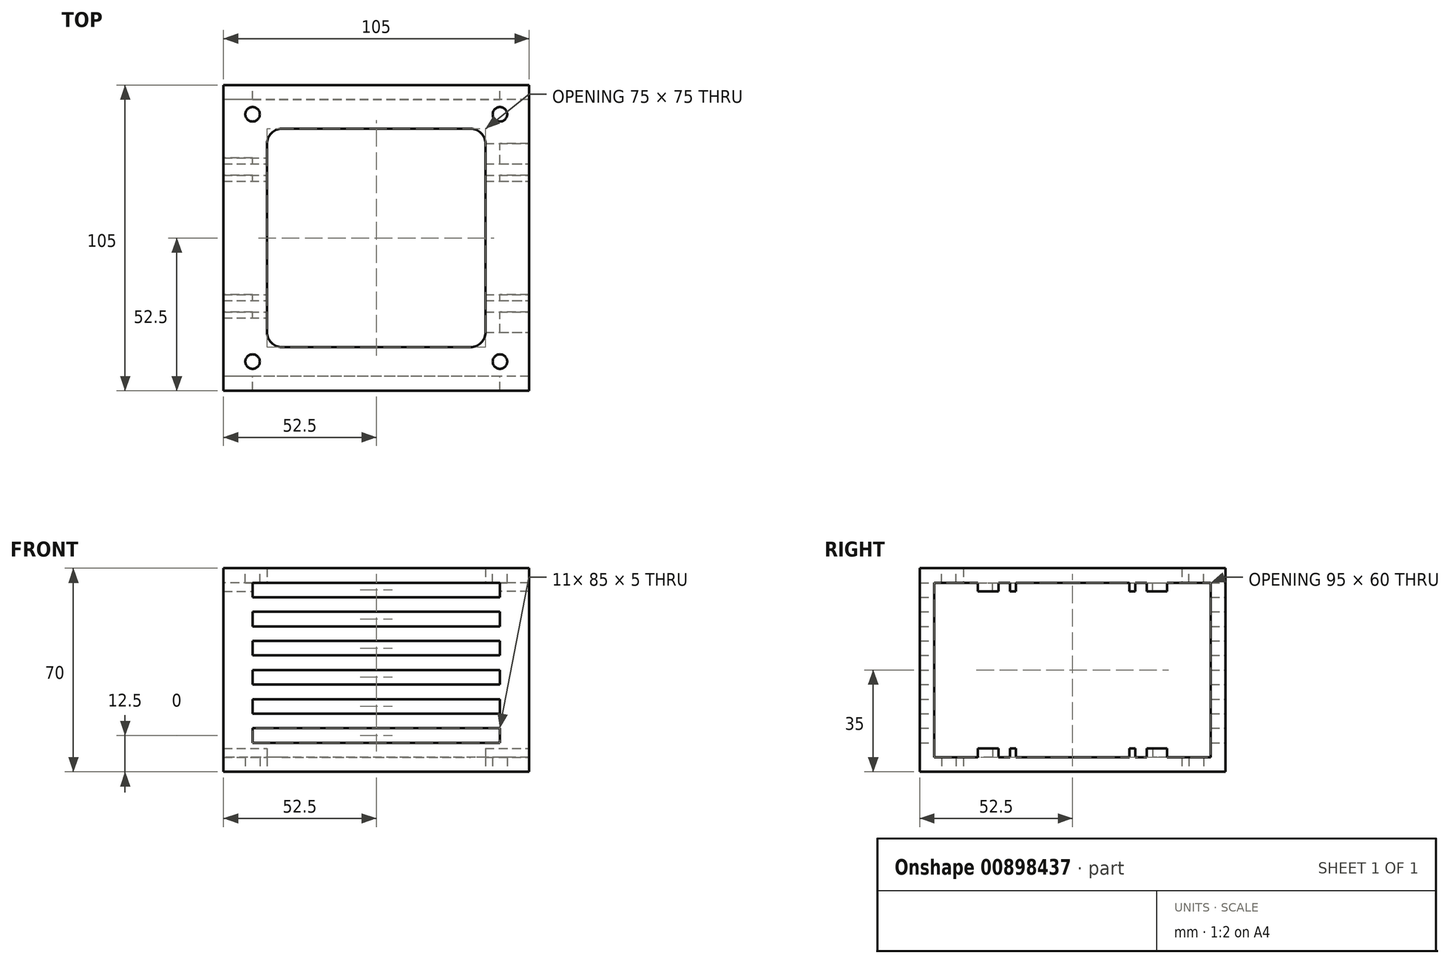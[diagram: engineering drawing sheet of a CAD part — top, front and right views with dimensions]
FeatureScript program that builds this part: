
annotation { "Feature Type Name" : "Feature", "Feature Type Description" : "" }
export const myFeature = defineFeature(function(context is Context, id is Id, definition is map)
    precondition{}
    {
        {
            var Q0;
            Q0=qCreatedBy(makeId("Top.planeOp"),FACE);
            var sketch = newSketch(context, id + "F0", { "sketchPlane" : qUnion([Q0])});
            skLineSegment(sketch, "E0.bottom", {"start": v(-52.5, 52.5) * mm, "end": v(52.5, 52.5) * mm});
            skLineSegment(sketch, "E0.top", {"start": v(-52.5, -52.5) * mm, "end": v(52.5, -52.5) * mm});
            skLineSegment(sketch, "E0.left", {"start": v(-52.5, 52.5) * mm, "end": v(-52.5, -52.5) * mm});
            skLineSegment(sketch, "E0.right", {"start": v(52.5, 52.5) * mm, "end": v(52.5, -52.5) * mm});
            skCircle(sketch, "E1", {"center": v(-42.5, 42.5) * mm, "radius": 2.5 * mm});
            skCircle(sketch, "E2.MirrorC", {"center": v(42.5, 42.5) * mm, "radius": 2.5 * mm});
            skCircle(sketch, "E3.MirrorC", {"center": v(-42.5, -42.5) * mm, "radius": 2.5 * mm});
            skCircle(sketch, "E4.MirrorC", {"center": v(42.5, -42.5) * mm, "radius": 2.5 * mm});
            skLineSegment(sketch, "E5.bottom", {"start": v(-32.5, 37.5) * mm, "end": v(32.5, 37.5) * mm});
            skLineSegment(sketch, "E5.top", {"start": v(-32.5, -37.5) * mm, "end": v(32.5, -37.5) * mm});
            skLineSegment(sketch, "E5.left", {"start": v(-37.5, 32.5) * mm, "end": v(-37.5, -32.5) * mm});
            skLineSegment(sketch, "E5.right", {"start": v(37.5, 32.5) * mm, "end": v(37.5, -32.5) * mm});
            skPoint(sketch, "E6.visualSharp", {"position": v(-37.5, 37.5) * mm});
            skArc(sketch, "E6.filletArc", {"start": v(-32.5, 37.5) * mm, "mid": v(-36.04, 36.04) * mm, "end": v(-37.5, 32.5) * mm});
            skPoint(sketch, "E7.visualSharp", {"position": v(-37.5, -37.5) * mm});
            skArc(sketch, "E7.filletArc", {"start": v(-37.5, -32.5) * mm, "mid": v(-36.04, -36.04) * mm, "end": v(-32.5, -37.5) * mm});
            skPoint(sketch, "E8.visualSharp", {"position": v(37.5, -37.5) * mm});
            skArc(sketch, "E8.filletArc", {"start": v(32.5, -37.5) * mm, "mid": v(36.04, -36.04) * mm, "end": v(37.5, -32.5) * mm});
            skPoint(sketch, "E9.visualSharp", {"position": v(37.5, 37.5) * mm});
            skArc(sketch, "E9.filletArc", {"start": v(37.5, 32.5) * mm, "mid": v(36.04, 36.04) * mm, "end": v(32.5, 37.5) * mm});
            skSolve(sketch);
        }
        {
            var Q0;
            Q0=makeQuery(id+"F0.imprint","IMPRINT",FACE,{"disambiguationData":[TD([[makeQuery(id+"F0.imprint","IMPRINT",EDGE,{"derivedFrom":sQuery(id+"F0.wireOp",EDGE,"E0.bottom")}),-1.0]])]});
            extrude(context, id + "F1", {"entities" : qUnion([Q0]), "depth" : 5 * mm, "offsetDistance" : 25 * mm});
        }
        {
            var Q0;
            Q0=makeQuery(id+"F1.opExtrude","CAP_FACE",FACE,{"disambiguationData":[OSD([sQuery(id+"F0.wireOp",EDGE,"E0.bottom"),sQuery(id+"F0.wireOp",EDGE,"E0.top"),sQuery(id+"F0.wireOp",EDGE,"E0.left"),sQuery(id+"F0.wireOp",EDGE,"E0.right"),sQuery(id+"F0.wireOp",EDGE,"E2.MirrorC"),sQuery(id+"F0.wireOp",EDGE,"E1"),sQuery(id+"F0.wireOp",EDGE,"E3.MirrorC"),sQuery(id+"F0.wireOp",EDGE,"E4.MirrorC"),sQuery(id+"F0.wireOp",EDGE,"E5.bottom"),sQuery(id+"F0.wireOp",EDGE,"E5.top"),sQuery(id+"F0.wireOp",EDGE,"E5.left"),sQuery(id+"F0.wireOp",EDGE,"E5.right"),sQuery(id+"F0.wireOp",EDGE,"E6.filletArc"),sQuery(id+"F0.wireOp",EDGE,"E7.filletArc"),sQuery(id+"F0.wireOp",EDGE,"E8.filletArc"),sQuery(id+"F0.wireOp",EDGE,"E9.filletArc")])],"isStart":false});
            var sketch = newSketch(context, id + "F2", { "sketchPlane" : qUnion([Q0])});
            skLineSegment(sketch, "E10.bottom", {"start": v(-52.5, 27.5) * mm, "end": v(-37.5, 27.5) * mm});
            skLineSegment(sketch, "E10.top", {"start": v(-52.5, 25.5) * mm, "end": v(-37.5, 25.5) * mm});
            skLineSegment(sketch, "E10.left", {"start": v(-52.5, 27.5) * mm, "end": v(-52.5, 25.5) * mm});
            skLineSegment(sketch, "E10.right", {"start": v(52.5, 32.5) * mm, "end": v(52.5, 25.5) * mm});
            skLineSegment(sketch, "E11.0", {"start": v(37.5, 32.5) * mm, "end": v(37.5, 25.5) * mm});
            skLineSegment(sketch, "E12.0", {"start": v(-37.5, 27.5) * mm, "end": v(-37.5, 25.5) * mm});
            skLineSegment(sketch, "E13.trimOffspring", {"start": v(37.5, 32.5) * mm, "end": v(52.5, 32.5) * mm});
            skLineSegment(sketch, "E14.trimOffspring", {"start": v(37.5, 25.5) * mm, "end": v(52.5, 25.5) * mm});
            skLineSegment(sketch, "E15.bottom", {"start": v(-52.5, 21.5) * mm, "end": v(-37.5, 21.5) * mm});
            skLineSegment(sketch, "E15.top", {"start": v(-52.5, 19.5) * mm, "end": v(-37.5, 19.5) * mm});
            skLineSegment(sketch, "E15.left", {"start": v(-52.5, 21.5) * mm, "end": v(-52.5, 19.5) * mm});
            skLineSegment(sketch, "E15.right", {"start": v(52.5, 21.5) * mm, "end": v(52.5, 19.5) * mm});
            skLineSegment(sketch, "E16.trimOffspring", {"start": v(37.5, 21.5) * mm, "end": v(52.5, 21.5) * mm});
            skLineSegment(sketch, "E17.trimOffspring", {"start": v(37.5, 19.5) * mm, "end": v(52.5, 19.5) * mm});
            skLineSegment(sketch, "E18.MirrorCS", {"start": v(-52.5, -27.5) * mm, "end": v(-37.5, -27.5) * mm});
            skLineSegment(sketch, "E19.MirrorCS", {"start": v(-52.5, -25.5) * mm, "end": v(-37.5, -25.5) * mm});
            skLineSegment(sketch, "E20.MirrorCS", {"start": v(-52.5, -21.5) * mm, "end": v(-37.5, -21.5) * mm});
            skLineSegment(sketch, "E21.MirrorCS", {"start": v(-52.5, -19.5) * mm, "end": v(-37.5, -19.5) * mm});
            skLineSegment(sketch, "E22.MirrorCS", {"start": v(37.5, -32.5) * mm, "end": v(52.5, -32.5) * mm});
            skLineSegment(sketch, "E23.MirrorCS", {"start": v(37.5, -25.5) * mm, "end": v(52.5, -25.5) * mm});
            skLineSegment(sketch, "E24.MirrorCS", {"start": v(37.5, -21.5) * mm, "end": v(52.5, -21.5) * mm});
            skLineSegment(sketch, "E25.MirrorCS", {"start": v(37.5, -19.5) * mm, "end": v(52.5, -19.5) * mm});
            skLineSegment(sketch, "E26.MirrorCS", {"start": v(37.5, -32.5) * mm, "end": v(37.5, -25.5) * mm});
            skLineSegment(sketch, "E27.MirrorCS", {"start": v(52.5, -21.5) * mm, "end": v(52.5, -19.5) * mm});
            skLineSegment(sketch, "E28.MirrorCS", {"start": v(52.5, -32.5) * mm, "end": v(52.5, -25.5) * mm});
            skLineSegment(sketch, "E29.MirrorCS", {"start": v(-52.5, -27.5) * mm, "end": v(-52.5, -25.5) * mm});
            skLineSegment(sketch, "E30.MirrorCS", {"start": v(-52.5, -21.5) * mm, "end": v(-52.5, -19.5) * mm});
            skLineSegment(sketch, "E31.MirrorCS", {"start": v(-37.5, -27.5) * mm, "end": v(-37.5, -25.5) * mm});
            skLineSegment(sketch, "E32.trimOffspring", {"start": v(-37.5, 21.5) * mm, "end": v(-37.5, 19.5) * mm});
            skLineSegment(sketch, "E33.trimOffspring", {"start": v(37.5, 21.5) * mm, "end": v(37.5, 19.5) * mm});
            skLineSegment(sketch, "E34.trimOffspring", {"start": v(37.5, -21.5) * mm, "end": v(37.5, -19.5) * mm});
            skLineSegment(sketch, "E35.trimOffspring", {"start": v(-37.5, -21.5) * mm, "end": v(-37.5, -19.5) * mm});
            skSolve(sketch);
        }
        {
            var Q0;
            Q0=makeQuery(id+"F2.imprint","IMPRINT",FACE,{"disambiguationData":[TD([[makeQuery(id+"F2.imprint","IMPRINT",EDGE,{"derivedFrom":sQuery(id+"F2.wireOp",EDGE,"E10.bottom")}),-1.0]])]});
            var Q1;
            Q1=makeQuery(id+"F2.imprint","IMPRINT",FACE,{"disambiguationData":[TD([[makeQuery(id+"F2.imprint","IMPRINT",EDGE,{"derivedFrom":sQuery(id+"F2.wireOp",EDGE,"E15.bottom")}),-1.0]])]});
            var Q2;
            Q2=makeQuery(id+"F2.imprint","IMPRINT",FACE,{"disambiguationData":[TD([[makeQuery(id+"F2.imprint","IMPRINT",EDGE,{"derivedFrom":sQuery(id+"F2.wireOp",EDGE,"E15.right")}),-1.0]])]});
            var Q3;
            Q3=makeQuery(id+"F2.imprint","IMPRINT",FACE,{"disambiguationData":[TD([[makeQuery(id+"F2.imprint","IMPRINT",EDGE,{"derivedFrom":sQuery(id+"F2.wireOp",EDGE,"E10.right")}),-1.0]])]});
            var Q4;
            Q4=makeQuery(id+"F2.imprint","IMPRINT",FACE,{"disambiguationData":[TD([[makeQuery(id+"F2.imprint","IMPRINT",EDGE,{"derivedFrom":sQuery(id+"F2.wireOp",EDGE,"E24.MirrorCS")}),1.0]])]});
            var Q5;
            Q5=makeQuery(id+"F2.imprint","IMPRINT",FACE,{"disambiguationData":[TD([[makeQuery(id+"F2.imprint","IMPRINT",EDGE,{"derivedFrom":sQuery(id+"F2.wireOp",EDGE,"E22.MirrorCS")}),1.0]])]});
            var Q6;
            Q6=makeQuery(id+"F2.imprint","IMPRINT",FACE,{"disambiguationData":[TD([[makeQuery(id+"F2.imprint","IMPRINT",EDGE,{"derivedFrom":sQuery(id+"F2.wireOp",EDGE,"E18.MirrorCS")}),1.0]])]});
            var Q7;
            Q7=makeQuery(id+"F2.imprint","IMPRINT",FACE,{"disambiguationData":[TD([[makeQuery(id+"F2.imprint","IMPRINT",EDGE,{"derivedFrom":sQuery(id+"F2.wireOp",EDGE,"E20.MirrorCS")}),1.0]])]});
            extrude(context, id + "F3", {"entities" : qUnion([Q0, Q1, Q2, Q3, Q4, Q5, Q6, Q7]), "operationType" : NewBodyOperationType.ADD, "depth" : 3 * mm, "offsetDistance" : 25 * mm});
        }
        {
            var Q0;
            Q0=qCreatedBy(makeId("Right.planeOp"),FACE);
            var sketch = newSketch(context, id + "F4", { "sketchPlane" : qUnion([Q0])});
            skLineSegment(sketch, "E36.0.4", {"start": v(52.5, 5) * mm, "end": v(47.5, 5) * mm});
            skLineSegment(sketch, "E37.0.7", {"start": v(-52.5, 5) * mm, "end": v(-47.5, 5) * mm});
            skLineSegment(sketch, "E38", {"start": v(52.5, 5) * mm, "end": v(52.5, 70) * mm});
            skLineSegment(sketch, "E39", {"start": v(52.5, 70) * mm, "end": v(-52.5, 70) * mm});
            skLineSegment(sketch, "E40", {"start": v(-52.5, 70) * mm, "end": v(-52.5, 5) * mm});
            skLineSegment(sketch, "E41", {"start": v(-47.5, 5) * mm, "end": v(-47.5, 65) * mm});
            skLineSegment(sketch, "E42", {"start": v(-47.5, 65) * mm, "end": v(47.5, 65) * mm});
            skLineSegment(sketch, "E43", {"start": v(47.5, 65) * mm, "end": v(47.5, 5) * mm});
            skLineSegment(sketch, "E44.trimOffspring", {"start": v(-47.5, 5) * mm, "end": v(-52.5, 5) * mm});
            skSolve(sketch);
        }
        {
            var Q0;
            Q0=makeQuery(id+"F4.imprint","IMPRINT",FACE,{"disambiguationData":[TD([[makeQuery(id+"F4.imprint","IMPRINT",EDGE,{"derivedFrom":sQuery(id+"F4.wireOp",EDGE,"E36.0.4")}),-1.0]])]});
            extrude(context, id + "F5", {"entities" : qUnion([Q0]), "operationType" : NewBodyOperationType.ADD, "depth" : (105 / 2) * mm, "offsetDistance" : 25 * mm, "hasSecondDirection" : true, "secondDirectionOppositeDirection" : true, "secondDirectionDepth" : 52.5 * mm});
        }
        {
            var Q0;
            Q0=makeQuery(id+"F5.opExtrude","SWEPT_FACE",FACE,{"disambiguationData":[OSD([sQuery(id+"F4.wireOp",EDGE,"E42")])]});
            var sketch = newSketch(context, id + "F6", { "sketchPlane" : qUnion([Q0])});
            skLineSegment(sketch, "E45.0", {"start": v(-32.5, -37.5) * mm, "end": v(32.5, -37.5) * mm});
            skArc(sketch, "E46.0", {"start": v(-32.5, -37.5) * mm, "mid": v(-36.04, -36.04) * mm, "end": v(-37.5, -32.5) * mm});
            skLineSegment(sketch, "E47.0", {"start": v(-37.5, -32.5) * mm, "end": v(-37.5, 32.5) * mm});
            skLineSegment(sketch, "E48.0", {"start": v(-32.5, 37.5) * mm, "end": v(32.5, 37.5) * mm});
            skArc(sketch, "E49.0", {"start": v(37.5, -32.5) * mm, "mid": v(36.04, -36.04) * mm, "end": v(32.5, -37.5) * mm});
            skArc(sketch, "E50.0", {"start": v(32.5, 37.5) * mm, "mid": v(36.04, 36.04) * mm, "end": v(37.5, 32.5) * mm});
            skArc(sketch, "E51.0", {"start": v(-37.5, 32.5) * mm, "mid": v(-36.04, 36.04) * mm, "end": v(-32.5, 37.5) * mm});
            skLineSegment(sketch, "E52.0", {"start": v(37.5, -32.5) * mm, "end": v(37.5, 32.5) * mm});
            skSolve(sketch);
        }
        {
            var Q0;
            Q0=makeQuery(id+"F6.imprint","IMPRINT",FACE,{"disambiguationData":[TD([[makeQuery(id+"F6.imprint","IMPRINT",EDGE,{"derivedFrom":sQuery(id+"F6.wireOp",EDGE,"E45.0")}),1.0]])]});
            extrude(context, id + "F7", {"entities" : qUnion([Q0]), "operationType" : NewBodyOperationType.REMOVE, "endBound" : BoundingType.UP_TO_NEXT, "oppositeDirection" : true, "depth" : 25 * mm, "offsetDistance" : 25 * mm});
        }
        {
            var Q0;
            Q0=makeQuery(id+"F5.opExtrude","SWEPT_FACE",FACE,{"disambiguationData":[OSD([sQuery(id+"F4.wireOp",EDGE,"E42")])]});
            var sketch = newSketch(context, id + "F8", { "sketchPlane" : qUnion([Q0])});
            skLineSegment(sketch, "E53.0.0", {"start": v(-52.5, -27.5) * mm, "end": v(-52.5, -25.5) * mm});
            skLineSegment(sketch, "E53.0.1", {"start": v(-52.5, -25.5) * mm, "end": v(-37.5, -25.5) * mm});
            skLineSegment(sketch, "E53.0.2", {"start": v(-37.5, -25.5) * mm, "end": v(-37.5, -27.5) * mm});
            skLineSegment(sketch, "E53.0.3", {"start": v(-37.5, -27.5) * mm, "end": v(-52.5, -27.5) * mm});
            skLineSegment(sketch, "E54.0.0", {"start": v(-52.5, -21.5) * mm, "end": v(-52.5, -19.5) * mm});
            skLineSegment(sketch, "E54.0.1", {"start": v(-52.5, -19.5) * mm, "end": v(-37.5, -19.5) * mm});
            skLineSegment(sketch, "E54.0.2", {"start": v(-37.5, -19.5) * mm, "end": v(-37.5, -21.5) * mm});
            skLineSegment(sketch, "E54.0.3", {"start": v(-37.5, -21.5) * mm, "end": v(-52.5, -21.5) * mm});
            skLineSegment(sketch, "E55.0.0", {"start": v(-37.5, 19.5) * mm, "end": v(-52.5, 19.5) * mm});
            skLineSegment(sketch, "E55.0.1", {"start": v(-52.5, 19.5) * mm, "end": v(-52.5, 21.5) * mm});
            skLineSegment(sketch, "E55.0.2", {"start": v(-52.5, 21.5) * mm, "end": v(-37.5, 21.5) * mm});
            skLineSegment(sketch, "E55.0.3", {"start": v(-37.5, 21.5) * mm, "end": v(-37.5, 19.5) * mm});
            skLineSegment(sketch, "E56.0.0", {"start": v(-37.5, 25.5) * mm, "end": v(-52.5, 25.5) * mm});
            skLineSegment(sketch, "E56.0.1", {"start": v(-52.5, 25.5) * mm, "end": v(-52.5, 27.5) * mm});
            skLineSegment(sketch, "E56.0.2", {"start": v(-52.5, 27.5) * mm, "end": v(-37.5, 27.5) * mm});
            skLineSegment(sketch, "E56.0.3", {"start": v(-37.5, 27.5) * mm, "end": v(-37.5, 25.5) * mm});
            skLineSegment(sketch, "E57.0.0", {"start": v(52.5, 25.5) * mm, "end": v(37.5, 25.5) * mm});
            skLineSegment(sketch, "E57.0.1", {"start": v(37.5, 25.5) * mm, "end": v(37.5, 32.5) * mm});
            skLineSegment(sketch, "E57.0.2", {"start": v(37.5, 32.5) * mm, "end": v(52.5, 32.5) * mm});
            skLineSegment(sketch, "E57.0.3", {"start": v(52.5, 32.5) * mm, "end": v(52.5, 25.5) * mm});
            skLineSegment(sketch, "E58.0.0", {"start": v(52.5, 19.5) * mm, "end": v(37.5, 19.5) * mm});
            skLineSegment(sketch, "E58.0.1", {"start": v(37.5, 19.5) * mm, "end": v(37.5, 21.5) * mm});
            skLineSegment(sketch, "E58.0.2", {"start": v(37.5, 21.5) * mm, "end": v(52.5, 21.5) * mm});
            skLineSegment(sketch, "E58.0.3", {"start": v(52.5, 21.5) * mm, "end": v(52.5, 19.5) * mm});
            skLineSegment(sketch, "E59.0.0", {"start": v(37.5, -32.5) * mm, "end": v(37.5, -25.5) * mm});
            skLineSegment(sketch, "E59.0.1", {"start": v(37.5, -25.5) * mm, "end": v(52.5, -25.5) * mm});
            skLineSegment(sketch, "E59.0.2", {"start": v(52.5, -25.5) * mm, "end": v(52.5, -32.5) * mm});
            skLineSegment(sketch, "E59.0.3", {"start": v(52.5, -32.5) * mm, "end": v(37.5, -32.5) * mm});
            skLineSegment(sketch, "E60.0.0", {"start": v(37.5, -21.5) * mm, "end": v(37.5, -19.5) * mm});
            skLineSegment(sketch, "E60.0.1", {"start": v(37.5, -19.5) * mm, "end": v(52.5, -19.5) * mm});
            skLineSegment(sketch, "E60.0.2", {"start": v(52.5, -19.5) * mm, "end": v(52.5, -21.5) * mm});
            skLineSegment(sketch, "E60.0.3", {"start": v(52.5, -21.5) * mm, "end": v(37.5, -21.5) * mm});
            skSolve(sketch);
        }
        {
            var Q0;
            Q0 = qSketchRegion(id + "F8", true);
            extrude(context, id + "F9", {"entities" : qUnion([Q0]), "operationType" : NewBodyOperationType.ADD, "depth" : 3 * mm, "offsetDistance" : 25 * mm});
        }
        {
            var Q0;
            Q0=makeQuery(id+"F5.boolean.opBoolean","MERGE",FACE,{"derivedFrom":[makeQuery(id+"F1.opExtrude","SWEPT_FACE",FACE,{"disambiguationData":[OSD([sQuery(id+"F0.wireOp",EDGE,"E0.bottom")])]}),makeQuery(id+"F5.opExtrude","SWEPT_FACE",FACE,{"disambiguationData":[OSD([sQuery(id+"F4.wireOp",EDGE,"E38")])]})]});
            var sketch = newSketch(context, id + "F10", { "sketchPlane" : qUnion([Q0])});
            skLineSegment(sketch, "E61.bottom", {"start": v(42.5, 10) * mm, "end": v(-42.5, 10) * mm});
            skLineSegment(sketch, "E61.top", {"start": v(42.5, 15) * mm, "end": v(-42.5, 15) * mm});
            skLineSegment(sketch, "E61.left", {"start": v(42.5, 10) * mm, "end": v(42.5, 15) * mm});
            skLineSegment(sketch, "E61.right", {"start": v(-42.5, 10) * mm, "end": v(-42.5, 15) * mm});
            skLineSegment(sketch, "E62.0.1.0", {"start": v(42.5, 20) * mm, "end": v(-42.5, 20) * mm});
            skLineSegment(sketch, "E62.0.1.1", {"start": v(42.5, 25) * mm, "end": v(-42.5, 25) * mm});
            skLineSegment(sketch, "E62.0.1.2", {"start": v(42.5, 20) * mm, "end": v(42.5, 25) * mm});
            skLineSegment(sketch, "E62.0.1.3", {"start": v(-42.5, 20) * mm, "end": v(-42.5, 25) * mm});
            skLineSegment(sketch, "E62.0.2.0", {"start": v(42.5, 30) * mm, "end": v(-42.5, 30) * mm});
            skLineSegment(sketch, "E62.0.2.1", {"start": v(42.5, 35) * mm, "end": v(-42.5, 35) * mm});
            skLineSegment(sketch, "E62.0.2.2", {"start": v(42.5, 30) * mm, "end": v(42.5, 35) * mm});
            skLineSegment(sketch, "E62.0.2.3", {"start": v(-42.5, 30) * mm, "end": v(-42.5, 35) * mm});
            skLineSegment(sketch, "E62.0.3.0", {"start": v(42.5, 40) * mm, "end": v(-42.5, 40) * mm});
            skLineSegment(sketch, "E62.0.3.1", {"start": v(42.5, 45) * mm, "end": v(-42.5, 45) * mm});
            skLineSegment(sketch, "E62.0.3.2", {"start": v(42.5, 40) * mm, "end": v(42.5, 45) * mm});
            skLineSegment(sketch, "E62.0.3.3", {"start": v(-42.5, 40) * mm, "end": v(-42.5, 45) * mm});
            skLineSegment(sketch, "E62.0.4.0", {"start": v(42.5, 50) * mm, "end": v(-42.5, 50) * mm});
            skLineSegment(sketch, "E62.0.4.1", {"start": v(42.5, 55) * mm, "end": v(-42.5, 55) * mm});
            skLineSegment(sketch, "E62.0.4.2", {"start": v(42.5, 50) * mm, "end": v(42.5, 55) * mm});
            skLineSegment(sketch, "E62.0.4.3", {"start": v(-42.5, 50) * mm, "end": v(-42.5, 55) * mm});
            skLineSegment(sketch, "E62.0.5.0", {"start": v(42.5, 60) * mm, "end": v(-42.5, 60) * mm});
            skLineSegment(sketch, "E62.0.5.1", {"start": v(42.5, 65) * mm, "end": v(-42.5, 65) * mm});
            skLineSegment(sketch, "E62.0.5.2", {"start": v(42.5, 60) * mm, "end": v(42.5, 65) * mm});
            skLineSegment(sketch, "E62.0.5.3", {"start": v(-42.5, 60) * mm, "end": v(-42.5, 65) * mm});
            skLineSegment(sketch, "E62.direction1", {"start": v(-42.5, 10) * mm, "end": v(-17.5, 10) * mm, "construction": true});
            skLineSegment(sketch, "E62.direction2", {"start": v(-42.5, 10) * mm, "end": v(-42.5, 20) * mm, "construction": true});
            skSolve(sketch);
        }
        {
            var Q0;
            Q0=makeQuery(id+"F10.imprint","IMPRINT",FACE,{"disambiguationData":[TD([[makeQuery(id+"F10.imprint","IMPRINT",EDGE,{"derivedFrom":sQuery(id+"F10.wireOp",EDGE,"E61.bottom")}),-1.0]])]});
            var Q1;
            Q1=makeQuery(id+"F10.imprint","IMPRINT",FACE,{"disambiguationData":[TD([[makeQuery(id+"F10.imprint","IMPRINT",EDGE,{"derivedFrom":sQuery(id+"F10.wireOp",EDGE,"E62.0.1.0")}),-1.0]])]});
            var Q2;
            Q2=makeQuery(id+"F10.imprint","IMPRINT",FACE,{"disambiguationData":[TD([[makeQuery(id+"F10.imprint","IMPRINT",EDGE,{"derivedFrom":sQuery(id+"F10.wireOp",EDGE,"E62.0.2.0")}),-1.0]])]});
            var Q3;
            Q3=makeQuery(id+"F10.imprint","IMPRINT",FACE,{"disambiguationData":[TD([[makeQuery(id+"F10.imprint","IMPRINT",EDGE,{"derivedFrom":sQuery(id+"F10.wireOp",EDGE,"E62.0.3.0")}),-1.0]])]});
            var Q4;
            Q4=makeQuery(id+"F10.imprint","IMPRINT",FACE,{"disambiguationData":[TD([[makeQuery(id+"F10.imprint","IMPRINT",EDGE,{"derivedFrom":sQuery(id+"F10.wireOp",EDGE,"E62.0.4.0")}),-1.0]])]});
            var Q5;
            Q5=makeQuery(id+"F10.imprint","IMPRINT",FACE,{"disambiguationData":[TD([[makeQuery(id+"F10.imprint","IMPRINT",EDGE,{"derivedFrom":sQuery(id+"F10.wireOp",EDGE,"E62.0.5.0")}),-1.0]])]});
            extrude(context, id + "F11", {"entities" : qUnion([Q0, Q1, Q2, Q3, Q4, Q5]), "operationType" : NewBodyOperationType.REMOVE, "endBound" : BoundingType.THROUGH_ALL, "oppositeDirection" : true, "depth" : 25 * mm, "offsetDistance" : 25 * mm});
        }
        {
            var Q0;
            Q0=makeQuery(id+"F5.opExtrude","SWEPT_FACE",FACE,{"disambiguationData":[OSD([sQuery(id+"F4.wireOp",EDGE,"E39")])]});
            var sketch = newSketch(context, id + "F12", { "sketchPlane" : qUnion([Q0])});
            skCircle(sketch, "E63.0", {"center": v(-42.5, 42.5) * mm, "radius": 2.5 * mm});
            skCircle(sketch, "E63.1", {"center": v(-42.5, -42.5) * mm, "radius": 2.5 * mm});
            skCircle(sketch, "E63.2", {"center": v(42.5, 42.5) * mm, "radius": 2.5 * mm});
            skCircle(sketch, "E63.3", {"center": v(42.5, -42.5) * mm, "radius": 2.5 * mm});
            skSolve(sketch);
        }
        {
            var Q0;
            Q0=makeQuery(id+"F12.imprint","IMPRINT",FACE,{"disambiguationData":[TD([[makeQuery(id+"F12.imprint","IMPRINT",EDGE,{"derivedFrom":sQuery(id+"F12.wireOp",EDGE,"E63.3")}),1.0]])]});
            var Q1;
            Q1=makeQuery(id+"F12.imprint","IMPRINT",FACE,{"disambiguationData":[TD([[makeQuery(id+"F12.imprint","IMPRINT",EDGE,{"derivedFrom":sQuery(id+"F12.wireOp",EDGE,"E63.1")}),1.0]])]});
            var Q2;
            Q2=makeQuery(id+"F12.imprint","IMPRINT",FACE,{"disambiguationData":[TD([[makeQuery(id+"F12.imprint","IMPRINT",EDGE,{"derivedFrom":sQuery(id+"F12.wireOp",EDGE,"E63.0")}),1.0]])]});
            var Q3;
            Q3=makeQuery(id+"F12.imprint","IMPRINT",FACE,{"disambiguationData":[TD([[makeQuery(id+"F12.imprint","IMPRINT",EDGE,{"derivedFrom":sQuery(id+"F12.wireOp",EDGE,"E63.2")}),1.0]])]});
            extrude(context, id + "F13", {"entities" : qUnion([Q0, Q1, Q2, Q3]), "operationType" : NewBodyOperationType.REMOVE, "oppositeDirection" : true, "depth" : 25 * mm, "offsetDistance" : 25 * mm});
        }
    });
